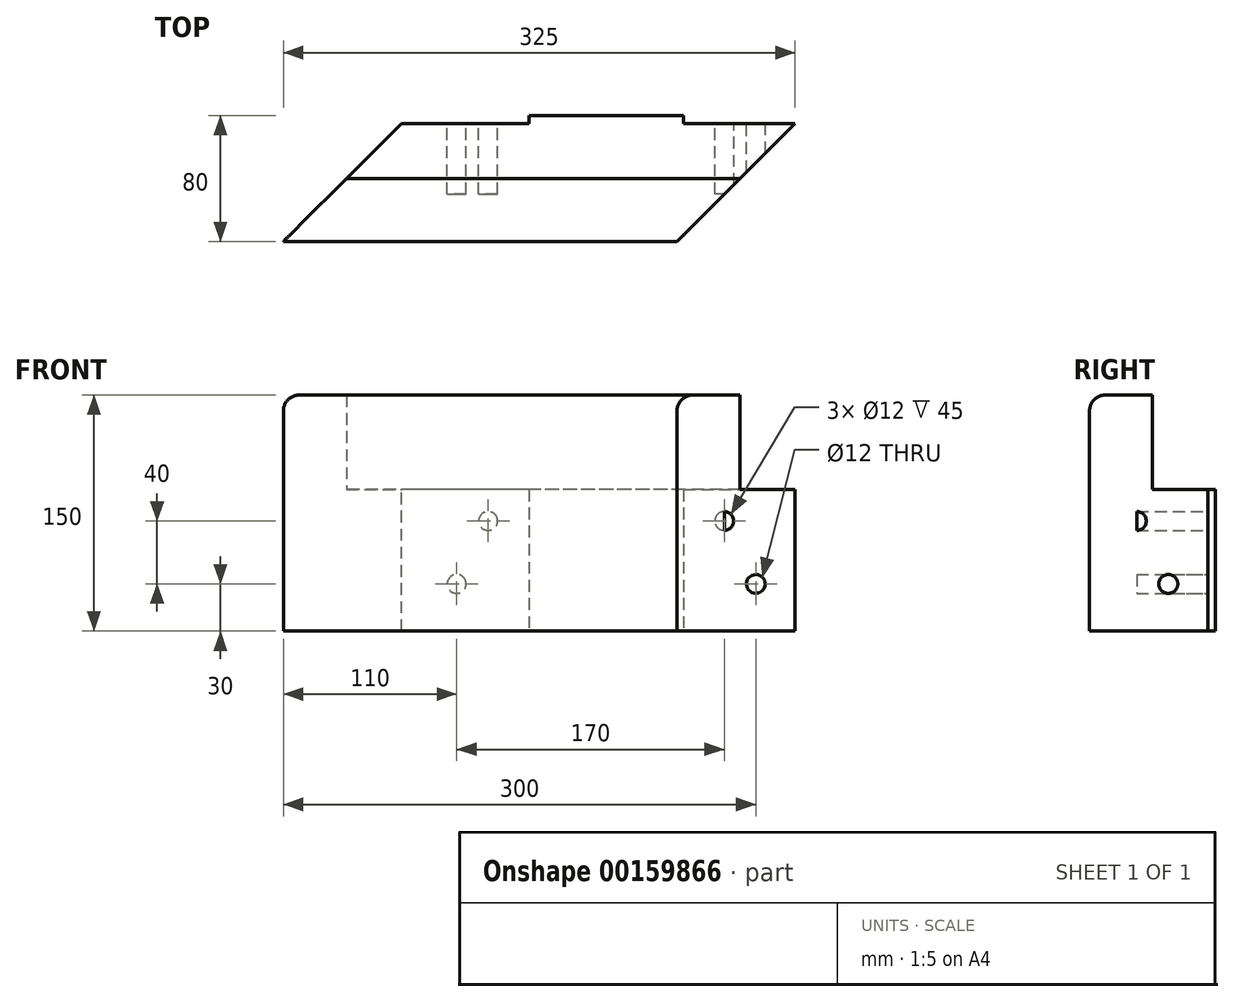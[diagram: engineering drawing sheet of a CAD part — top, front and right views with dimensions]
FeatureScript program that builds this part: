
annotation { "Feature Type Name" : "Feature", "Feature Type Description" : "" }
export const myFeature = defineFeature(function(context is Context, id is Id, definition is map)
    precondition{}
    {
        {
            assignVariable(context, id + "F0", {"name" : "L", "anyValue" : 280 * mm + 50 * mm});
        }
        {
            assignVariable(context, id + "F1", {"name" : "B", "anyValue" : 80 * mm});
        }
        {
            var Q0;
            Q0=qCreatedBy(makeId("Right.planeOp"),FACE);
            var sketch = newSketch(context, id + "F2", { "sketchPlane" : qUnion([Q0])});
            skLineSegment(sketch, "E0.bottom", {"start": v(-40, -75) * mm, "end": v(40, -75) * mm});
            skLineSegment(sketch, "E0.top", {"start": v(-40, 75) * mm, "end": v(0, 75) * mm});
            skLineSegment(sketch, "E0.left", {"start": v(-40, -75) * mm, "end": v(-40, 75) * mm});
            skLineSegment(sketch, "E0.right", {"start": v(40, -75) * mm, "end": v(40, 15) * mm});
            skPoint(sketch, "E0.middle", {"position": v(0, 0) * mm});
            skLineSegment(sketch, "E1", {"start": v(0, 75) * mm, "end": v(0, 15) * mm});
            skLineSegment(sketch, "E2", {"start": v(0, 15) * mm, "end": v(40, 15) * mm});
            skSolve(sketch);
        }
        {
            var Q0;
            Q0=qSketchRegion(id+"F2",true);
            extrude(context, id + "F3", {"entities" : qUnion([Q0]), "endBound" : BoundingType.SYMMETRIC, "depth" : getVariable(context, 'L')});
        }
        {
            var Q0;
            Q0=makeQuery(id+"F3.opExtrude","CAP_EDGE",EDGE,{"disambiguationData":[OSD([sQuery(id+"F2.wireOp",EDGE,"E0.right")])],"isStart":true});
            var Q1;
            Q1=makeQuery(id+"F3.opExtrude","CAP_EDGE",EDGE,{"disambiguationData":[OSD([sQuery(id+"F2.wireOp",EDGE,"E0.left")])],"isStart":false});
            chamfer(context, id + "F4", {"entities" : qUnion([Q0, Q1]), "width" : getVariable(context, 'B'), "tangentPropagation" : true});
        }
        {
            var Q0;
            Q0=makeQuery(id+"F3.opExtrude","SWEPT_FACE",FACE,{"disambiguationData":[OSD([sQuery(id+"F2.wireOp",EDGE,"E0.right")])]});
            var sketch = newSketch(context, id + "F5", { "sketchPlane" : qUnion([Q0])});
            skCircle(sketch, "E3.MirrorC", {"center": v(35, -5) * mm, "radius": 6 * mm});
            skCircle(sketch, "E4.MirrorC", {"center": v(55, -45) * mm, "radius": 6 * mm});
            skLineSegment(sketch, "E5", {"start": v(-40, 15) * mm, "end": v(-40, -75) * mm, "construction": true});
            skCircle(sketch, "E6.MirrorC", {"center": v(-115, -5) * mm, "radius": 6 * mm});
            skCircle(sketch, "E7.MirrorC", {"center": v(-135, -45) * mm, "radius": 6 * mm});
            skSolve(sketch);
        }
        {
            var Q0;
            Q0=qSketchRegion(id+"F5",true);
            extrude(context, id + "F6", {"entities" : qUnion([Q0]), "operationType" : NewBodyOperationType.REMOVE, "oppositeDirection" : true, "depth" : getVariable(context, 'B') - 30 * mm});
        }
        {
            var Q0;
            Q0=makeQuery(id+"F3.opExtrude","SWEPT_FACE",FACE,{"disambiguationData":[OSD([sQuery(id+"F2.wireOp",EDGE,"E0.right")])]});
            var sketch = newSketch(context, id + "F7", { "sketchPlane" : qUnion([Q0])});
            skLineSegment(sketch, "E8.bottom", {"start": v(9, 15) * mm, "end": v(125, 15) * mm});
            skLineSegment(sketch, "E8.top", {"start": v(9, -75) * mm, "end": v(125, -75) * mm});
            skLineSegment(sketch, "E8.left", {"start": v(9, 15) * mm, "end": v(9, -75) * mm});
            skLineSegment(sketch, "E8.right", {"start": v(125, 15) * mm, "end": v(125, -75) * mm});
            skLineSegment(sketch, "E9", {"start": v(-40, 15) * mm, "end": v(-40, -75) * mm, "construction": true});
            skLineSegment(sketch, "E10.MirrorCS", {"start": v(-89, 15) * mm, "end": v(-89, -75) * mm});
            skLineSegment(sketch, "E11.MirrorCS", {"start": v(-89, 15) * mm, "end": v(-205, 15) * mm});
            skLineSegment(sketch, "E12.MirrorCS", {"start": v(-205, 15) * mm, "end": v(-205, -75) * mm});
            skLineSegment(sketch, "E13.MirrorCS", {"start": v(-89, -75) * mm, "end": v(-205, -75) * mm});
            skSolve(sketch);
        }
        {
            var Q0;
            Q0=qSketchRegion(id+"F7",true);
            extrude(context, id + "F8", {"entities" : qUnion([Q0]), "operationType" : NewBodyOperationType.REMOVE, "oppositeDirection" : true, "depth" : 5 * mm});
        }
        {
            var Q0;
            Q0=makeQuery(id+"F3.opExtrude","SWEPT_EDGE",EDGE,{"disambiguationData":[OSD([sQuery(id+"F2.wireOp",EDGE,"E0.top"),sQuery(id+"F2.wireOp",EDGE,"E0.left")])]});
            fillet(context, id + "F9", {"entities" : qUnion([Q0]), "radius" : 10 * mm, "tangentPropagation" : true, "allowEdgeOverflow" : false});
        }
    });
